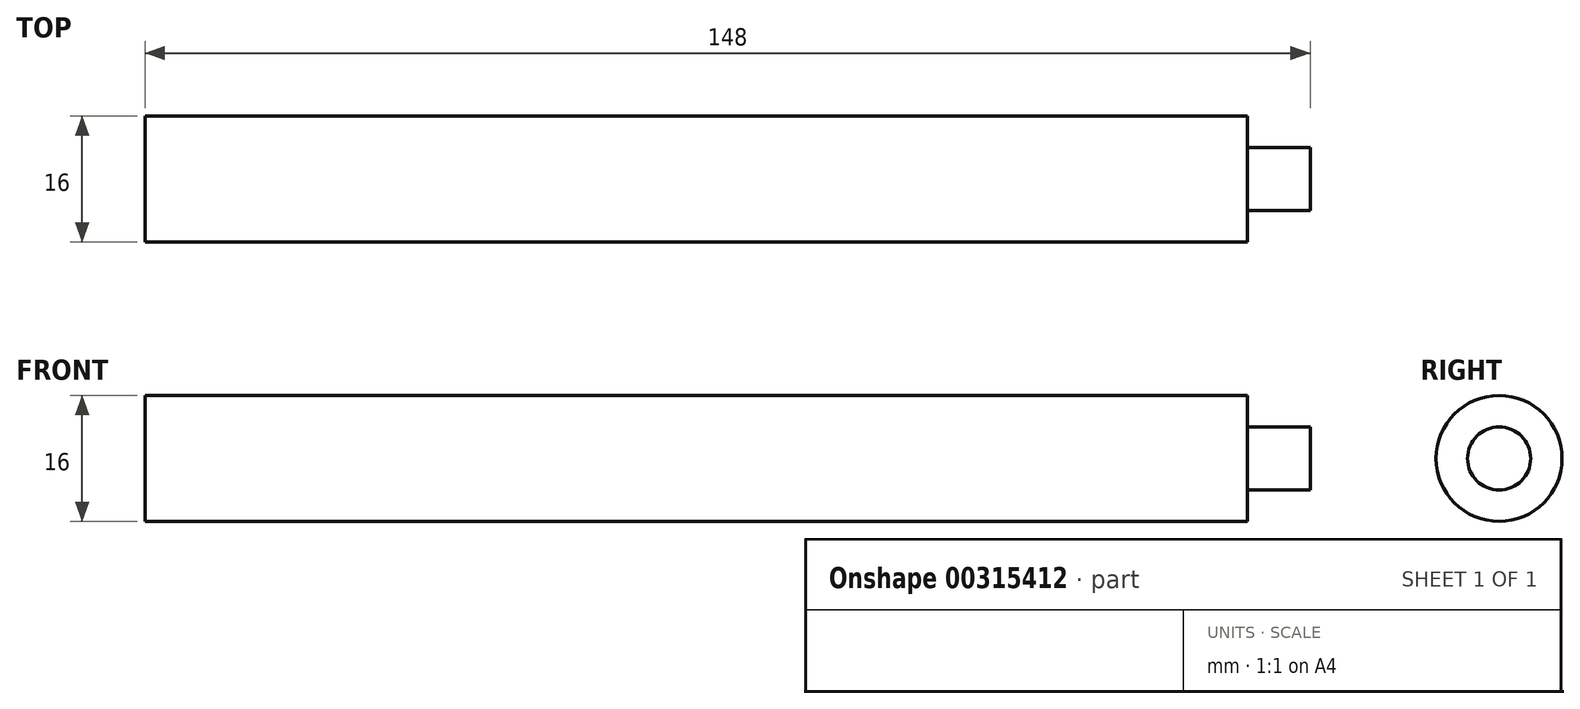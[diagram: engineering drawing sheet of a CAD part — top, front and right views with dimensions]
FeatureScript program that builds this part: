
annotation { "Feature Type Name" : "Feature", "Feature Type Description" : "" }
export const myFeature = defineFeature(function(context is Context, id is Id, definition is map)
    precondition{}
    {
        {
            var Q0;
            Q0=qCreatedBy(makeId("Right.planeOp"),FACE);
            var sketch = newSketch(context, id + "F0", { "sketchPlane" : qUnion([Q0])});
            skCircle(sketch, "E0", {"center": v(0, 0) * mm, "radius": 8 * mm});
            skSolve(sketch);
        }
        {
            var Q0;
            Q0=qSketchRegion(id+"F0",true);
            extrude(context, id + "F1", {"entities" : qUnion([Q0]), "endBound" : BoundingType.SYMMETRIC, "depth" : 80 * mm});
        }
        {
            var Q0;
            Q0=makeQuery(id+"F1.opExtrude","CAP_FACE",FACE,{"disambiguationData":[OSD([sQuery(id+"F0.wireOp",EDGE,"E0")])],"isStart":false});
            var sketch = newSketch(context, id + "F2", { "sketchPlane" : qUnion([Q0])});
            skCircle(sketch, "E1", {"center": v(0, 0) * mm, "radius": 4 * mm});
            skSolve(sketch);
        }
        {
            var Q0;
            Q0=qSketchRegion(id+"F2",true);
            extrude(context, id + "F3", {"entities" : qUnion([Q0]), "operationType" : NewBodyOperationType.ADD, "depth" : 8 * mm});
        }
        {
            var Q0;
            Q0=makeQuery(id+"F1.opExtrude","CAP_FACE",FACE,{"disambiguationData":[OSD([sQuery(id+"F0.wireOp",EDGE,"E0")])],"isStart":true});
            var sketch = newSketch(context, id + "F4", { "sketchPlane" : qUnion([Q0])});
            skSolve(sketch);
        }
        {
            var Q0;
            Q0=makeQuery(id+"F4.imprint","IMPRINT",FACE,{"disambiguationData":[TD([[makeQuery(id+"F4.imprint","IMPRINT",EDGE,{"derivedFrom":makeQuery(id+"F1.opExtrude","CAP_EDGE",EDGE,{"disambiguationData":[OSD([sQuery(id+"F0.wireOp",EDGE,"E0")])],"isStart":true})}),-1.0]])]});
            extrude(context, id + "F5", {"entities" : qUnion([Q0]), "operationType" : NewBodyOperationType.ADD, "depth" : 60 * mm});
        }
    });
